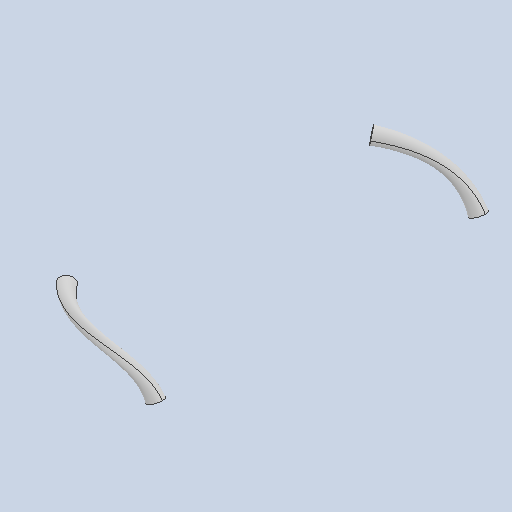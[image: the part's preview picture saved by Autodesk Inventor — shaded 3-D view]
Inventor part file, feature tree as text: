
AUTODESK INVENTOR PART (.ipt)
format: ipt  version: 2025.2 (Build 292293000, 293)  size: 176,640 bytes
history: native  units: mm
features: other x2, loft x2
ambient origin geometry x8: Origin, YZ Plane, XZ Plane, XY Plane, X Axis, Y Axis, Z Axis, Center Point
bodies: Body1 (feature_tree), Body2 (feature_tree)
feature tree (4):
  other  "Bryła1"
  other  "Bryła2"
  loft  "Loft1"
  loft  "Loft2"
